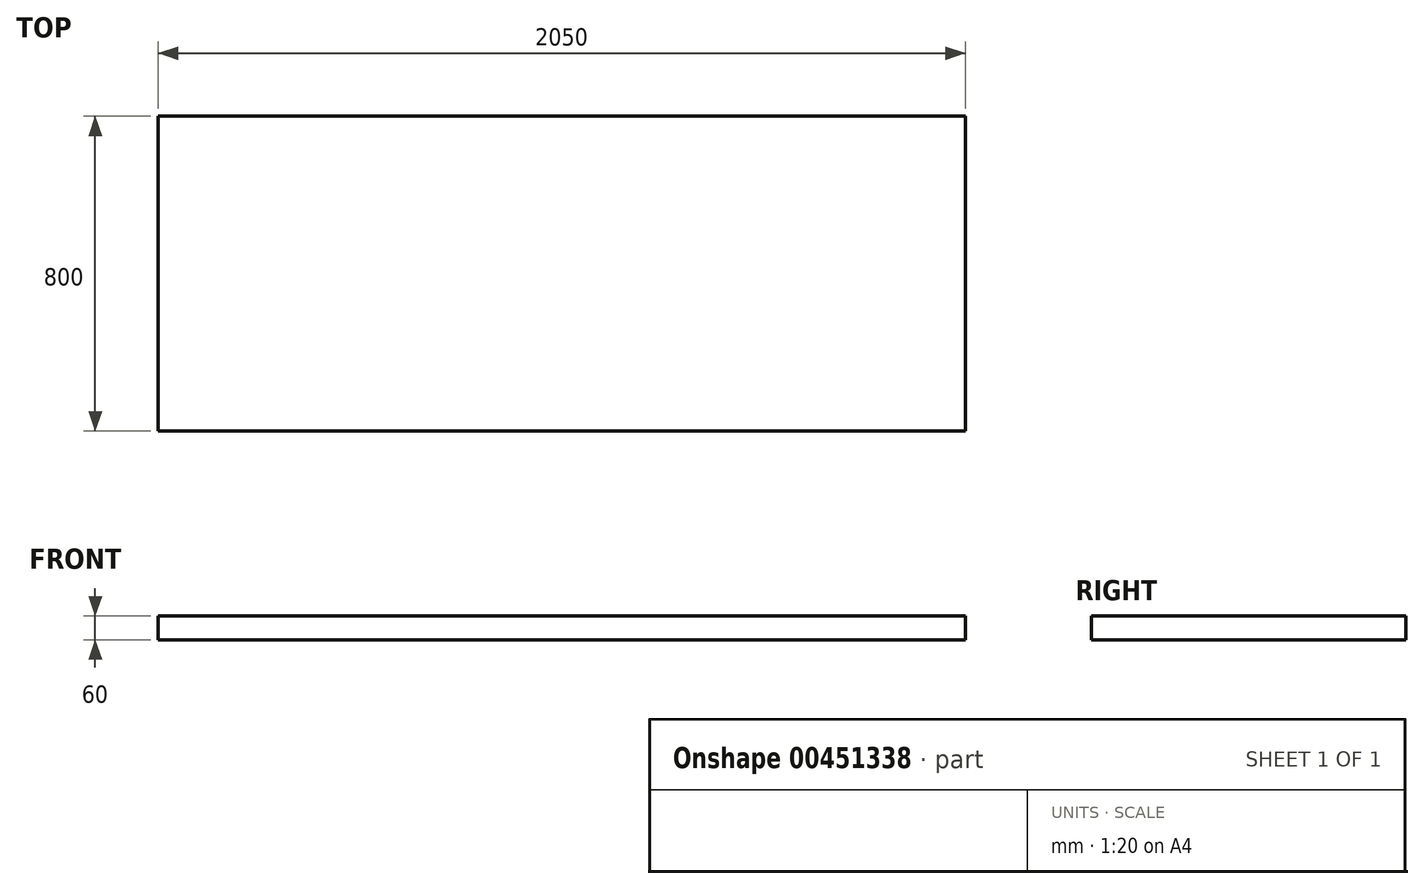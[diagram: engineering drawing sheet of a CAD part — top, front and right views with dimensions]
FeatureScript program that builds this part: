
annotation { "Feature Type Name" : "Feature", "Feature Type Description" : "" }
export const myFeature = defineFeature(function(context is Context, id is Id, definition is map)
    precondition{}
    {
        {
            var Q0;
            Q0=qCreatedBy(makeId("Top.planeOp"),FACE);
            var sketch = newSketch(context, id + "F0", { "sketchPlane" : qUnion([Q0])});
            skLineSegment(sketch, "E0.bottom", {"start": v(1025, 400) * mm, "end": v(-1025, 400) * mm});
            skLineSegment(sketch, "E0.top", {"start": v(1025, -400) * mm, "end": v(-1025, -400) * mm});
            skLineSegment(sketch, "E0.left", {"start": v(1025, 400) * mm, "end": v(1025, -400) * mm});
            skLineSegment(sketch, "E0.right", {"start": v(-1025, 400) * mm, "end": v(-1025, -400) * mm});
            skPoint(sketch, "E0.middle", {"position": v(0, 0) * mm});
            skSolve(sketch);
        }
        {
            var Q0;
            Q0=makeQuery(id+"F0.imprint","IMPRINT",FACE,{"disambiguationData":[TD([[makeQuery(id+"F0.imprint","IMPRINT",EDGE,{"derivedFrom":sQuery(id+"F0.wireOp",EDGE,"E0.bottom")}),1.0]])]});
            extrude(context, id + "F1", {"entities" : qUnion([Q0]), "depth" : 60 * mm});
        }
    });
